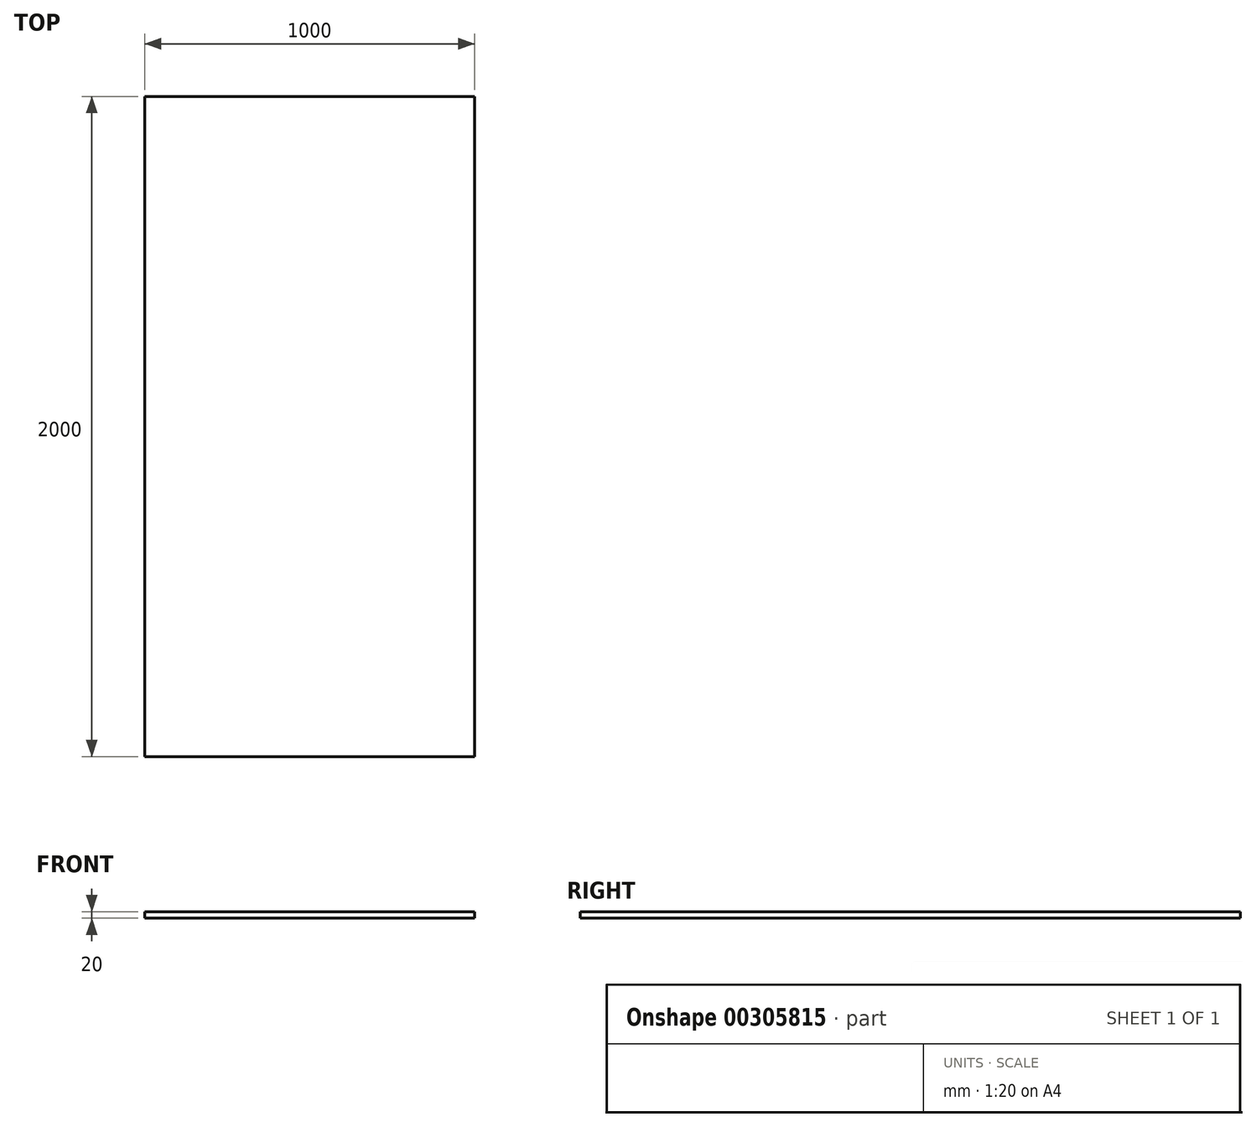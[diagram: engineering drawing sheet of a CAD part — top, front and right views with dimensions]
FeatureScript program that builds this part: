
annotation { "Feature Type Name" : "Feature", "Feature Type Description" : "" }
export const myFeature = defineFeature(function(context is Context, id is Id, definition is map)
    precondition{}
    {
        {
            var Q0;
            Q0=qCreatedBy(makeId("Front.planeOp"),FACE);
            var sketch = newSketch(context, id + "F0", { "sketchPlane" : qUnion([Q0])});
            skLineSegment(sketch, "E0.bottom", {"start": v(-33.6, 29.8) * mm, "end": v(966.4, 29.8) * mm});
            skLineSegment(sketch, "E0.top", {"start": v(-33.6, 9.8) * mm, "end": v(966.4, 9.8) * mm});
            skLineSegment(sketch, "E0.left", {"start": v(-33.6, 29.8) * mm, "end": v(-33.6, 9.8) * mm});
            skLineSegment(sketch, "E0.right", {"start": v(966.4, 29.8) * mm, "end": v(966.4, 9.8) * mm});
            skSolve(sketch);
        }
        {
            var Q0;
            Q0 = qSketchRegion(id + "F0", true);
            extrude(context, id + "F1", {"entities" : qUnion([Q0]), "depth" : 2000 * mm});
        }
    });
